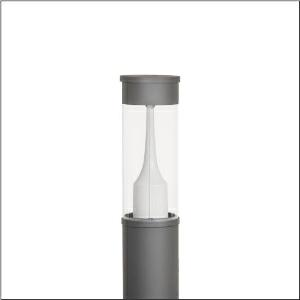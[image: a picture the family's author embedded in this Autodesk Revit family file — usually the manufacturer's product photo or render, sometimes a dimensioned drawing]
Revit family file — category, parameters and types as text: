
# Revit family: city-light_120_iq___p1_0a_5xa5285bf14h_8c15
name_source: partatom
category: Lighting Fixtures
units: mm (PartAtom-declared; Revit-internal decimal feet)

## family parameters
Cut with Voids When Loaded = No
Host = Face
Light Source = No
Part Type = Normal
Room Calculation Point = No
Round Connector Dimension = Use Diameter
Shared = No

## types (1)
- --- (1 x LED, 1510 lm, 12.9 W, 2200K)
    Apparent Load = 13 VA
    CIE Flux Codes = 32 61 90 93 100
    Color Rendering = 70
    Color Temperature = 2200K
    Default Elevation = 1800 mm
    Description = City-Light 120 iQ, bollard luminaire, Module 540 iQ-SR, primary light control with 3 zone facetted reflector, of plastic, silver coated, highly specular, structured, primary optical cover: cover, of PMMA, transparent, partly coated, light distribution: P1.0a, primary light characteristic: strongly asymmetric, LED, High Power LED, rated luminous flux: 1.510lm, luminous efficacy: 117lm/W, light colour: 722, colour temperature: 2200K, control gear: ECG iQ, control: presetting dimming logarithmic, Street-Remote, Auto-Match, Temp-Guard, Lumen-Switch, Night-Set, Smart-Wire, Light-Fading, Desk-Remote (wireless, voltage-free reading and setting of iQ features in the workshop via application-optimized NFC function/RFID function), optimised constant luminous flux control (CLO 2.0), with terminal, 6-pole, max. 2.5mm², mains connection: 230..240V, AC, 50/60Hz, start of lifetime: 13W, end of service life: 13W, reduction: 6W, luminaire housing, cylindrical, of extruded aluminium section, coated, Siteco® metallic grey (DB 702S), length: 1.200mm, diameter: 200mm, Module 540 iQ-SR, traffic white (RAL 9016), equipment: standard, protection rating (complete): IP54, insulation class (complete): insulation class II (safety insulation), certification: CE, ENEC, VDE, packaging unit: 1 piece

Light Distribution: P1.0a
    Height = 500 mm
    Lamp = 1 x LED
    Lamp Light Flux = 1510 lm
    Lamp Power = 12.9 W
    Lamp count = 1
    Length = 200 mm  [stored 0.656168 ft]
    Luminous efficacy = 117 lm/W
    Manufacturer = Siteco
    ModVariant = No
    Model = 5XA5285BF14H
    Mounting Place = Floor
    Mounting Type = Freestanding
    Number of Poles = 1
    OnlyDefault = Yes
    Power Factor = 1
    Product Name = City-Light 120 iQ | P1.0a
    Product group = bollard luminaire
    ProductGroupID = 1304
    Protection Class = Protection class II
    Protection Degree = IP 54
    RLX_Detail_Level = 1
    RLX_Emergency_Light_Flux = 0 lm
    RLX_Emergency_Type = 0
    RLX_Emergency_Type_DB = No
    RlxData = <blob elided: 53145 chars, md5=463201e9>
    Socket = socket
    Standby Power = 0 W
    System Light Flux = 1510 lm
    System Power = 13 W
    Type Comments = factory setting: luminous flux: 100 % | dim-lin: 254 | 516 mA
    Type Image = l_1006922.jpg
    URL = http://relux.com
    VarID = @adj_091951
    Voltage = 0 V
    Weight = 0.00 kg
    Width = 0 mm  [stored 0 ft]

note: [stored X ft] marks values corroborated as IEEE doubles in the binary element streams (Revit-internal decimal feet)

## geometry (parser evidence)
native form markers: Blend x4, Sweep x11
no freeform markers — native parametric forms only
